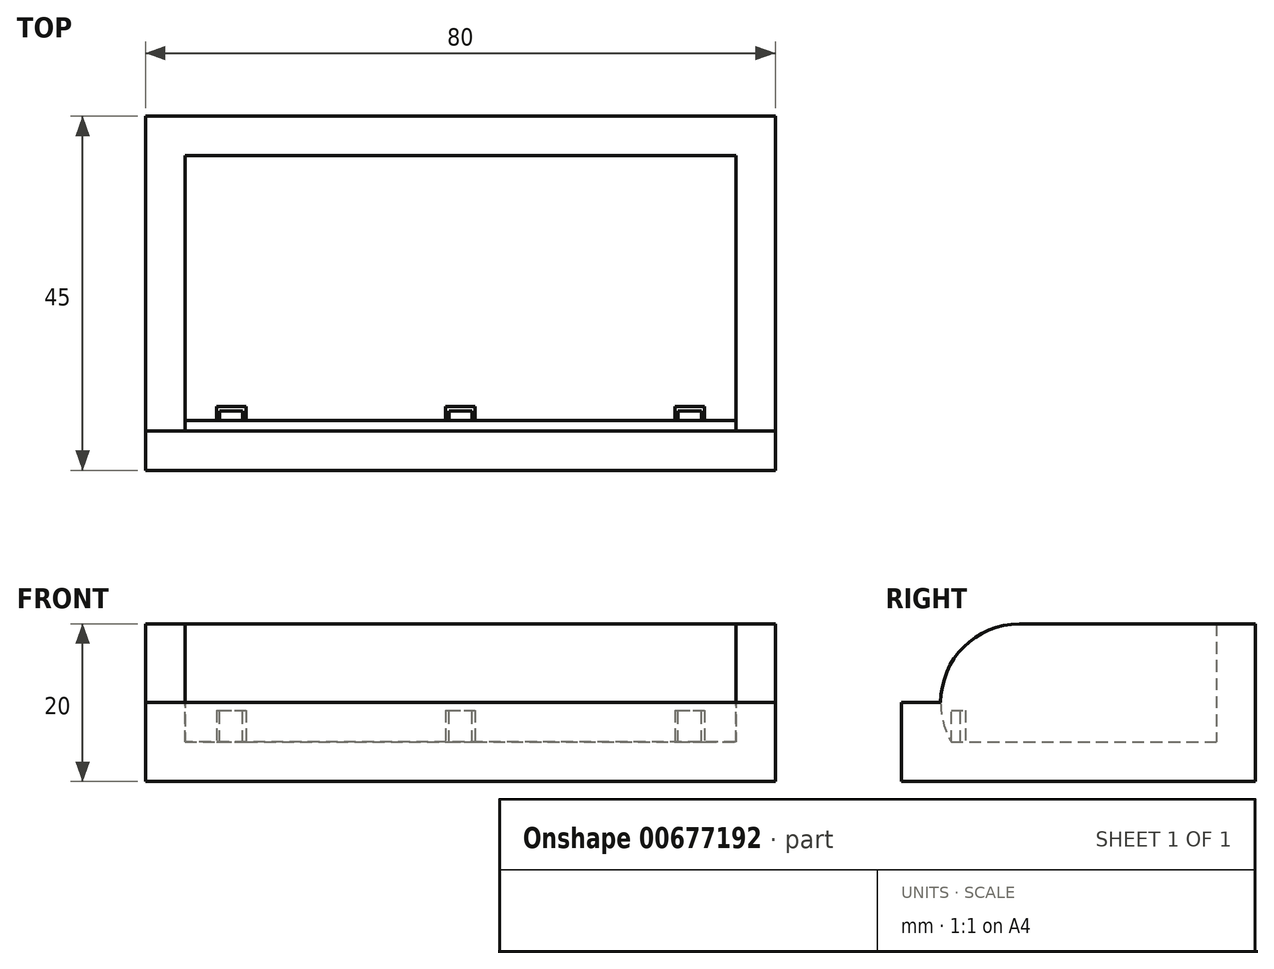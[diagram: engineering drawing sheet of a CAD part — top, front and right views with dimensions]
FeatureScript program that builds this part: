
annotation { "Feature Type Name" : "Feature", "Feature Type Description" : "" }
export const myFeature = defineFeature(function(context is Context, id is Id, definition is map)
    precondition{}
    {
        {
            var Q0;
            Q0=qCreatedBy(makeId("Top.planeOp"),FACE);
            var sketch = newSketch(context, id + "F0", { "sketchPlane" : qUnion([Q0])});
            skLineSegment(sketch, "E0.bottom", {"start": v(40, -22.5) * mm, "end": v(-40, -22.5) * mm});
            skLineSegment(sketch, "E0.top", {"start": v(40, 22.5) * mm, "end": v(-40, 22.5) * mm});
            skLineSegment(sketch, "E0.left", {"start": v(40, -22.5) * mm, "end": v(40, 22.5) * mm});
            skLineSegment(sketch, "E0.right", {"start": v(-40, -22.5) * mm, "end": v(-40, 22.5) * mm});
            skPoint(sketch, "E0.middle", {"position": v(0, 0) * mm});
            skSolve(sketch);
        }
        {
            var Q0;
            Q0 = qSketchRegion(id + "F0", true);
            extrude(context, id + "F1", {"entities" : qUnion([Q0]), "endBound" : BoundingType.SYMMETRIC, "depth" : 25 * mm, "offsetDistance" : 25 * mm});
        }
        {
            var Q0;
            Q0=makeQuery(id+"F1.opExtrude","CAP_EDGE",EDGE,{"disambiguationData":[OSD([sQuery(id+"F0.wireOp",EDGE,"E0.bottom")])],"isStart":false});
            fillet(context, id + "F2", {"entities" : qUnion([Q0]), "radius" : 15 * mm, "tangentPropagation" : true, "allowEdgeOverflow" : false});
        }
        {
            var Q0;
            Q0=makeQuery(id+"F1.opExtrude","CAP_EDGE",EDGE,{"disambiguationData":[OSD([sQuery(id+"F0.wireOp",EDGE,"E0.top")])],"isStart":false});
            fillet(context, id + "F3", {"entities" : qUnion([Q0]), "radius" : 5 * mm, "tangentPropagation" : true, "allowEdgeOverflow" : false});
        }
        {
            var Q0;
            Q0=makeQuery(id+"F1.opExtrude","SWEPT_FACE",FACE,{"disambiguationData":[OSD([sQuery(id+"F0.wireOp",EDGE,"E0.left")])]});
            var sketch = newSketch(context, id + "F4", { "sketchPlane" : qUnion([Q0])});
            skLineSegment(sketch, "E1", {"start": v(22.5, 7.5) * mm, "end": v(-7.5, 7.5) * mm});
            skLineSegment(sketch, "E2", {"start": v(-22.5, -2.5) * mm, "end": v(-17.5, -2.5) * mm});
            skArc(sketch, "E3", {"start": v(-7.5, 7.5) * mm, "mid": v(-14.57, 4.57) * mm, "end": v(-17.5, -2.5) * mm});
            skArc(sketch, "E4.0.1", {"start": v(22.5, 7.5) * mm, "mid": v(21.04, 11.04) * mm, "end": v(17.5, 12.5) * mm});
            skLineSegment(sketch, "E4.0.2", {"start": v(17.5, 12.5) * mm, "end": v(-7.5, 12.5) * mm});
            skArc(sketch, "E4.0.3", {"start": v(-7.5, 12.5) * mm, "mid": v(-18.1, 8.1) * mm, "end": v(-22.5, -2.5) * mm});
            skPoint(sketch, "E4.0.5.start.orphan", {"position": v(-22.5, -12.5) * mm});
            skPoint(sketch, "E4.0.0.start.orphan", {"position": v(22.5, -12.5) * mm});
            skSolve(sketch);
        }
        {
            var Q0;
            Q0 = qSketchRegion(id + "F4", true);
            extrude(context, id + "F5", {"entities" : qUnion([Q0]), "operationType" : NewBodyOperationType.REMOVE, "endBound" : BoundingType.THROUGH_ALL, "oppositeDirection" : true, "depth" : 25 * mm, "offsetDistance" : 25 * mm});
        }
        {
            var Q0;
            Q0=makeQuery(id+"F5.boolean.opBoolean","COPY",FACE,{"derivedFrom":makeQuery(id+"F5.opExtrude","SWEPT_FACE",FACE,{"disambiguationData":[OSD([sQuery(id+"F4.wireOp",EDGE,"E1")])]})});
            var Q1;
            Q1=makeQuery(id+"F5.boolean.opBoolean","COPY",FACE,{"derivedFrom":makeQuery(id+"F5.opExtrude","SWEPT_FACE",FACE,{"disambiguationData":[OSD([sQuery(id+"F4.wireOp",EDGE,"E3")])]})});
            shell(context, id + "F6", {"entities" : qUnion([Q0, Q1]), "thickness" : 5 * mm});
        }
        {
            var Q0;
            Q0=makeQuery(id+"F6.opShell","OFFSET_FACE",FACE,{"disambiguationData":[OSD([sQuery(id+"F0.wireOp",EDGE,"E0.bottom"),sQuery(id+"F0.wireOp",EDGE,"E0.top"),sQuery(id+"F0.wireOp",EDGE,"E0.left"),sQuery(id+"F0.wireOp",EDGE,"E0.right")])]});
            var sketch = newSketch(context, id + "F7", { "sketchPlane" : qUnion([Q0])});
            skLineSegment(sketch, "E5.bottom", {"start": v(-31, -16.16) * mm, "end": v(-27.25, -16.16) * mm});
            skLineSegment(sketch, "E5.top", {"start": v(-31, -14.36) * mm, "end": v(-27.25, -14.36) * mm});
            skLineSegment(sketch, "E5.left", {"start": v(-31, -16.16) * mm, "end": v(-31, -14.36) * mm});
            skLineSegment(sketch, "E5.right", {"start": v(-27.25, -16.16) * mm, "end": v(-27.25, -14.36) * mm});
            skLineSegment(sketch, "E6.bottom", {"start": v(-1.87, -16.16) * mm, "end": v(1.88, -16.16) * mm});
            skLineSegment(sketch, "E6.top", {"start": v(-1.88, -14.36) * mm, "end": v(1.88, -14.36) * mm});
            skLineSegment(sketch, "E6.left", {"start": v(-1.87, -16.16) * mm, "end": v(-1.88, -14.36) * mm});
            skLineSegment(sketch, "E6.right", {"start": v(1.88, -16.16) * mm, "end": v(1.88, -14.36) * mm});
            skLineSegment(sketch, "E7.bottom", {"start": v(27.25, -16.16) * mm, "end": v(31, -16.16) * mm});
            skLineSegment(sketch, "E7.top", {"start": v(27.25, -14.36) * mm, "end": v(31, -14.36) * mm});
            skLineSegment(sketch, "E7.left", {"start": v(27.25, -16.16) * mm, "end": v(27.25, -14.36) * mm});
            skLineSegment(sketch, "E7.right", {"start": v(31, -16.16) * mm, "end": v(31, -14.36) * mm});
            skSolve(sketch);
        }
        {
            var Q0;
            Q0 = qSketchRegion(id + "F7", true);
            extrude(context, id + "F8", {"entities" : qUnion([Q0]), "operationType" : NewBodyOperationType.ADD, "depth" : 4 * mm, "offsetDistance" : 25 * mm});
        }
        {
            var Q0;
            Q0=makeQuery(id+"F8.opExtrude","CAP_FACE",FACE,{"disambiguationData":[OSD([sQuery(id+"F7.wireOp",EDGE,"E5.bottom"),sQuery(id+"F7.wireOp",EDGE,"E5.top"),sQuery(id+"F7.wireOp",EDGE,"E5.left"),sQuery(id+"F7.wireOp",EDGE,"E5.right")])],"isStart":false});
            var sketch = newSketch(context, id + "F9", { "sketchPlane" : qUnion([Q0])});
            skLineSegment(sketch, "E8", {"start": v(-30.6, -16.16) * mm, "end": v(-30.6, -14.96) * mm});
            skLineSegment(sketch, "E9", {"start": v(-30.6, -14.96) * mm, "end": v(-27.65, -14.96) * mm});
            skLineSegment(sketch, "E10", {"start": v(-27.65, -14.96) * mm, "end": v(-27.65, -16.16) * mm});
            skLineSegment(sketch, "E11.0", {"start": v(-30.6, -16.16) * mm, "end": v(-27.65, -16.16) * mm});
            skPoint(sketch, "E12.orphan", {"position": v(-31, -16.16) * mm});
            skPoint(sketch, "E13.orphan", {"position": v(-27.25, -16.16) * mm});
            skSolve(sketch);
        }
        {
            var Q0;
            Q0 = qSketchRegion(id + "F9", true);
            extrude(context, id + "F10", {"entities" : qUnion([Q0]), "operationType" : NewBodyOperationType.REMOVE, "oppositeDirection" : true, "depth" : 4 * mm, "offsetDistance" : 25 * mm});
        }
        {
            var Q0;
            Q0=makeQuery(id+"F8.opExtrude","CAP_FACE",FACE,{"disambiguationData":[OSD([sQuery(id+"F7.wireOp",EDGE,"E6.bottom"),sQuery(id+"F7.wireOp",EDGE,"E6.top"),sQuery(id+"F7.wireOp",EDGE,"E6.left"),sQuery(id+"F7.wireOp",EDGE,"E6.right")])],"isStart":false});
            var sketch = newSketch(context, id + "F11", { "sketchPlane" : qUnion([Q0])});
            skLineSegment(sketch, "E14", {"start": v(-1.47, -16.16) * mm, "end": v(-1.47, -14.96) * mm});
            skLineSegment(sketch, "E15", {"start": v(-1.47, -14.96) * mm, "end": v(1.47, -14.96) * mm});
            skLineSegment(sketch, "E16", {"start": v(1.47, -14.96) * mm, "end": v(1.47, -16.16) * mm});
            skLineSegment(sketch, "E17", {"start": v(1.47, -16.16) * mm, "end": v(-1.47, -16.16) * mm});
            skSolve(sketch);
        }
        {
            var Q0;
            Q0 = qSketchRegion(id + "F11", true);
            extrude(context, id + "F12", {"entities" : qUnion([Q0]), "operationType" : NewBodyOperationType.REMOVE, "oppositeDirection" : true, "depth" : 4 * mm, "offsetDistance" : 25 * mm});
        }
        {
            var Q0;
            Q0=makeQuery(id+"F8.opExtrude","CAP_FACE",FACE,{"disambiguationData":[OSD([sQuery(id+"F7.wireOp",EDGE,"E7.bottom"),sQuery(id+"F7.wireOp",EDGE,"E7.top"),sQuery(id+"F7.wireOp",EDGE,"E7.left"),sQuery(id+"F7.wireOp",EDGE,"E7.right")])],"isStart":false});
            var sketch = newSketch(context, id + "F13", { "sketchPlane" : qUnion([Q0])});
            skLineSegment(sketch, "E18", {"start": v(27.65, -16.16) * mm, "end": v(27.65, -14.96) * mm});
            skLineSegment(sketch, "E19", {"start": v(27.65, -14.96) * mm, "end": v(30.6, -14.96) * mm});
            skLineSegment(sketch, "E20", {"start": v(30.6, -14.96) * mm, "end": v(30.6, -16.16) * mm});
            skLineSegment(sketch, "E21", {"start": v(30.6, -16.16) * mm, "end": v(27.65, -16.16) * mm});
            skSolve(sketch);
        }
        {
            var Q0;
            Q0 = qSketchRegion(id + "F13", true);
            extrude(context, id + "F14", {"entities" : qUnion([Q0]), "operationType" : NewBodyOperationType.REMOVE, "oppositeDirection" : true, "depth" : 4 * mm, "offsetDistance" : 25 * mm});
        }
    });
